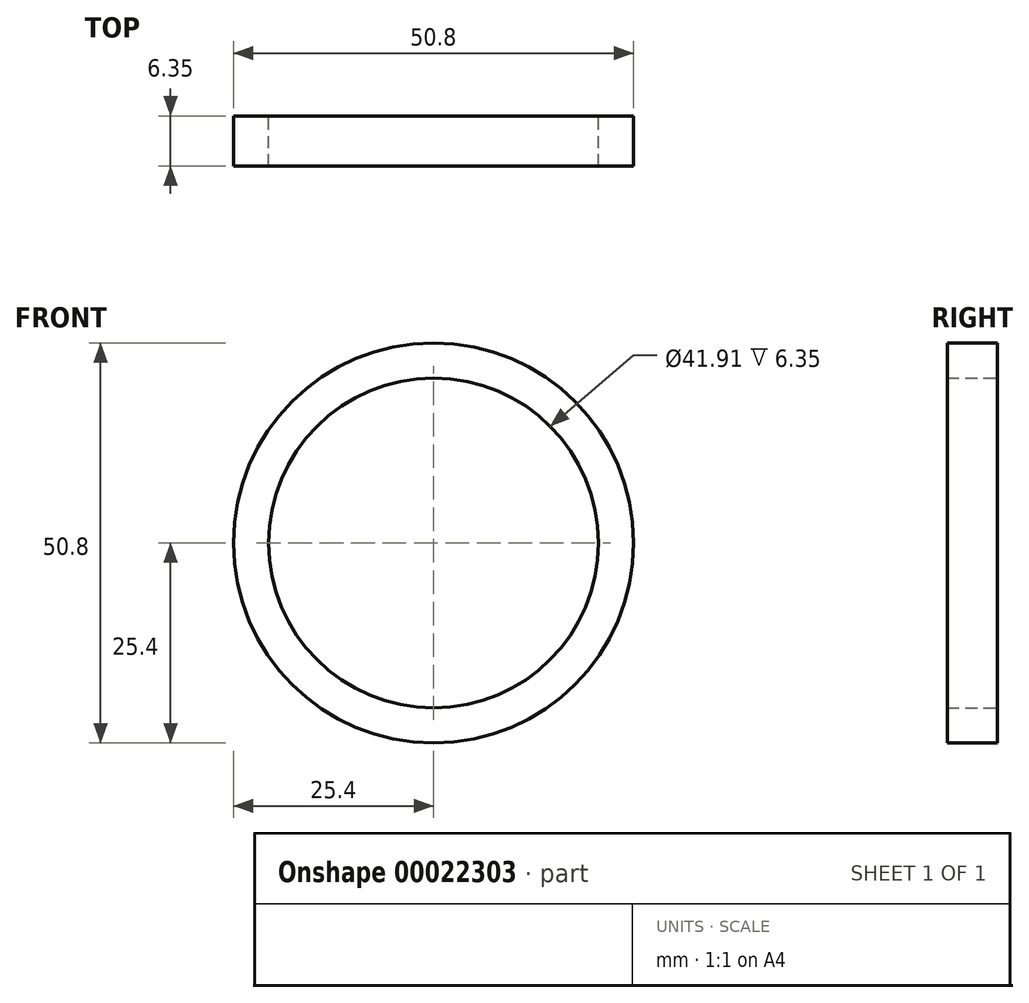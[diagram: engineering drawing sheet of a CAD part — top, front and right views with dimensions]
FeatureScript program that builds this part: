
annotation { "Feature Type Name" : "Feature", "Feature Type Description" : "" }
export const myFeature = defineFeature(function(context is Context, id is Id, definition is map)
    precondition{}
    {
        {
            var Q0;
            Q0=qCreatedBy(makeId("Front.planeOp"),FACE);
            var sketch = newSketch(context, id + "F0", { "sketchPlane" : qUnion([Q0])});
            skCircle(sketch, "E0", {"center": v(0, 0) * mm, "radius": 25.4 * mm});
            skCircle(sketch, "E1", {"center": v(0, 0) * mm, "radius": 20.96 * mm});
            skSolve(sketch);
        }
        {
            var Q0;
            Q0=sQuery(id+"F0.wireOp",EDGE,"E0");
            extrude(context, id + "F1", {"bodyType" : ToolBodyType.SURFACE, "surfaceEntities" : qUnion([Q0]), "depth" : 6.35 * mm});
        }
        {
            var Q0;
            Q0=qCreatedBy(makeId("Front.planeOp"),FACE);
            var sketch = newSketch(context, id + "F2", { "sketchPlane" : qUnion([Q0])});
            skCircle(sketch, "E2", {"center": v(0, 0) * mm, "radius": 25.4 * mm});
            skCircle(sketch, "E3", {"center": v(0, 0) * mm, "radius": 20.96 * mm});
            skSolve(sketch);
        }
        {
            var Q0;
            Q0=makeQuery(id+"F2.imprint","IMPRINT",FACE,{"disambiguationData":[TD([[makeQuery(id+"F2.imprint","IMPRINT",EDGE,{"derivedFrom":sQuery(id+"F2.wireOp",EDGE,"E2")}),1.0]])]});
            extrude(context, id + "F3", {"entities" : qUnion([Q0]), "depth" : 6.35 * mm});
        }
    });
